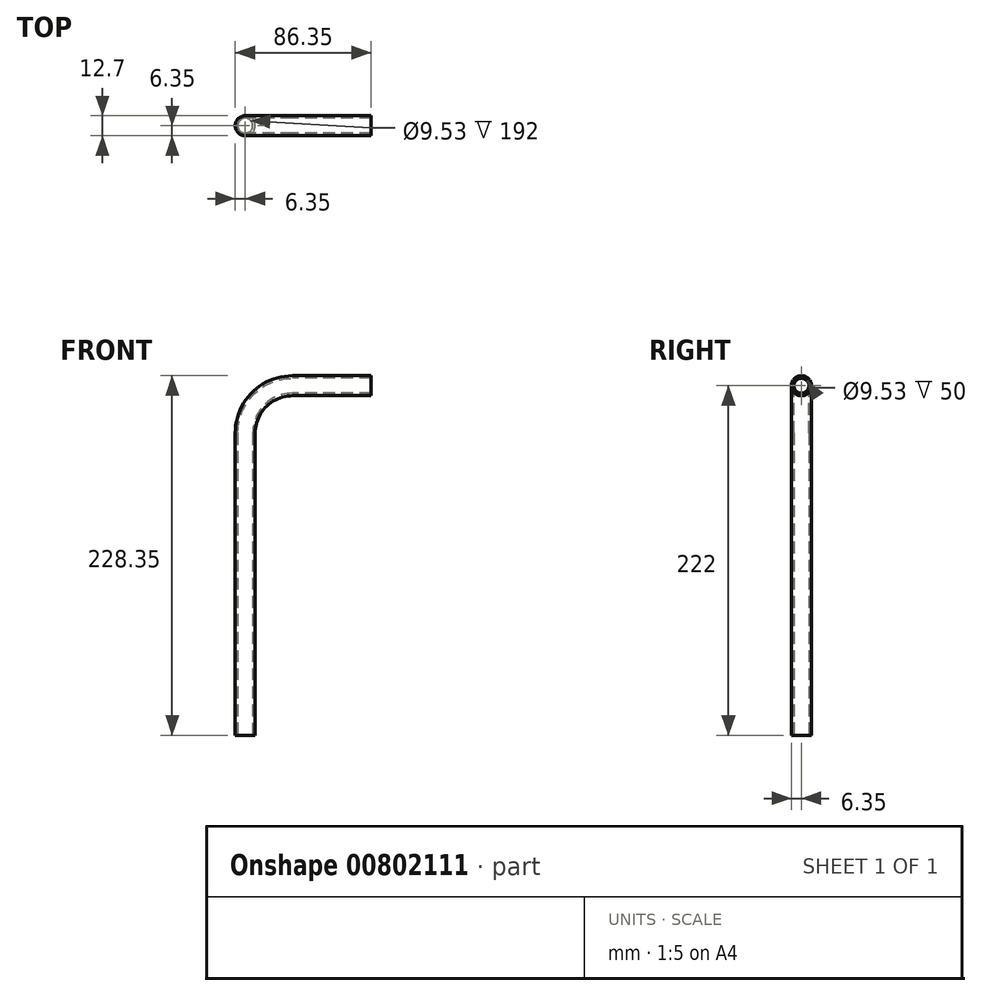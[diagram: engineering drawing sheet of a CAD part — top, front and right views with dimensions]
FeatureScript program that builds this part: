
annotation { "Feature Type Name" : "Feature", "Feature Type Description" : "" }
export const myFeature = defineFeature(function(context is Context, id is Id, definition is map)
    precondition{}
    {
        {
            var Q0;
            Q0=qCreatedBy(makeId("Front.planeOp"),FACE);
            var sketch = newSketch(context, id + "F0", { "sketchPlane" : qUnion([Q0])});
            skLineSegment(sketch, "E0", {"start": v(0, 0) * mm, "end": v(-50, 0) * mm});
            skLineSegment(sketch, "E1", {"start": v(-80, -30) * mm, "end": v(-80, -222) * mm});
            skPoint(sketch, "E2.visualSharp", {"position": v(-80, 0) * mm});
            skArc(sketch, "E2.filletArc", {"start": v(-50, 0) * mm, "mid": v(-71.21, -8.79) * mm, "end": v(-80, -30) * mm});
            skSolve(sketch);
        }
        {
            var Q0;
            Q0=qCreatedBy(makeId("Right.planeOp"),FACE);
            var sketch = newSketch(context, id + "F1", { "sketchPlane" : qUnion([Q0])});
            skCircle(sketch, "E3", {"center": v(0, 0) * mm, "radius": 6.35 * mm});
            skCircle(sketch, "E4", {"center": v(0, 0) * mm, "radius": 4.76 * mm});
            skSolve(sketch);
        }
        {
            var Q0;
            Q0=qSketchRegion(id+"F1",true);
            var Q1;
            Q1=qConstructionFilter(qBodyType(qCreatedBy(id+"F0",EDGE),BodyType.WIRE),ConstructionObject.NO);
            sweep(context, id + "F2", {"profiles" : qUnion([Q0]), "path" : qUnion([Q1])});
        }
    });
